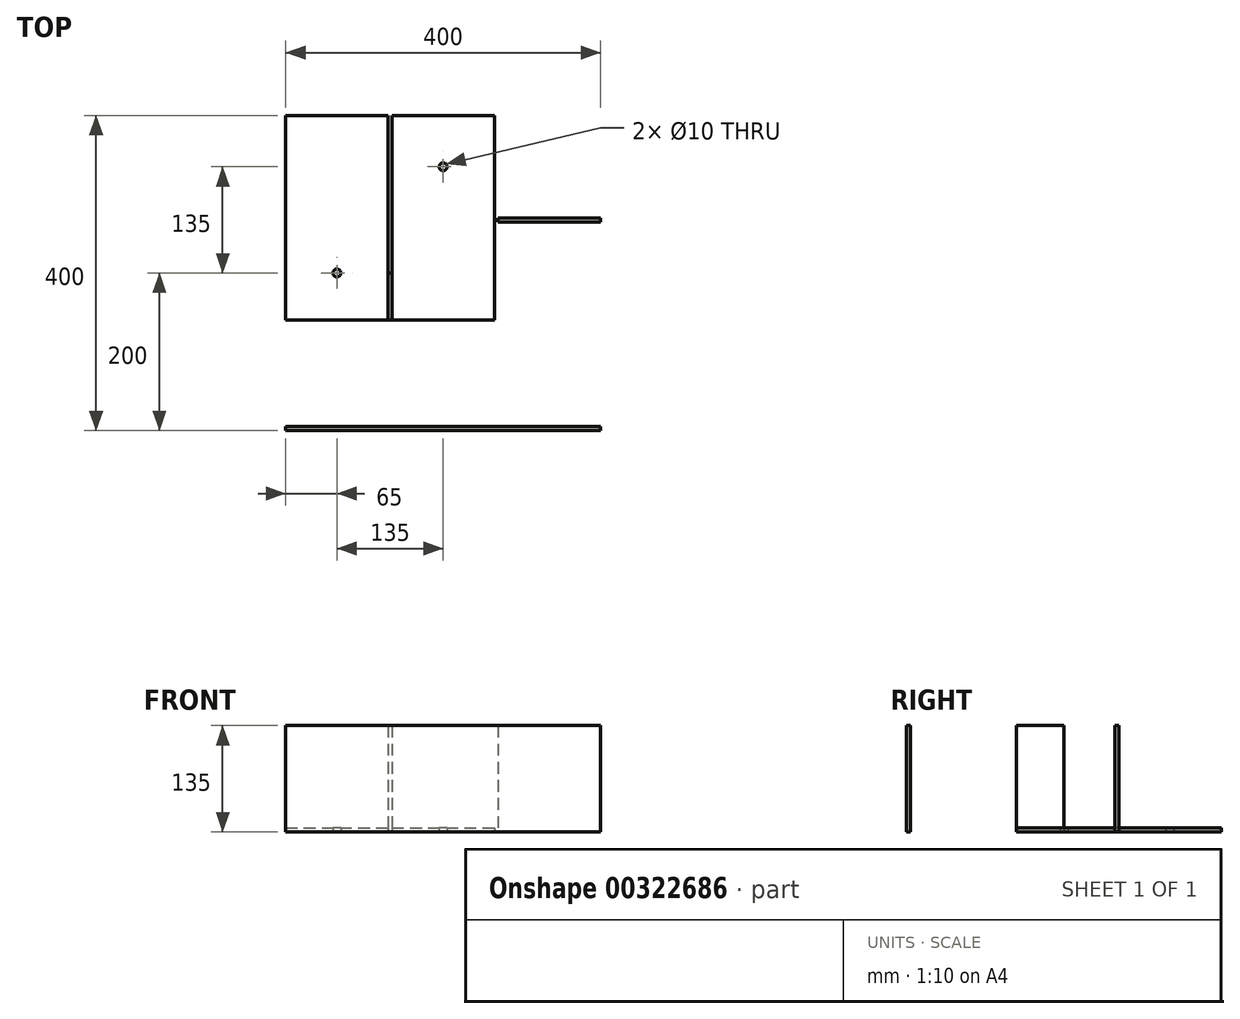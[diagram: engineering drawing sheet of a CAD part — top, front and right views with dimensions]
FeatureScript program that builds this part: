
annotation { "Feature Type Name" : "Feature", "Feature Type Description" : "" }
export const myFeature = defineFeature(function(context is Context, id is Id, definition is map)
    precondition{}
    {
        {
            var Q0;
            Q0=qCreatedBy(makeId("Top.planeOp"),FACE);
            var sketch = newSketch(context, id + "F0", { "sketchPlane" : qUnion([Q0])});
            skLineSegment(sketch, "E0", {"start": v(0, 0) * mm, "end": v(-200, 0) * mm});
            skLineSegment(sketch, "E1", {"start": v(-200, 0) * mm, "end": v(-200, 200) * mm});
            skLineSegment(sketch, "E2", {"start": v(-200, 0) * mm, "end": v(-200, -200) * mm});
            skLineSegment(sketch, "E3.bottom", {"start": v(-200, 200) * mm, "end": v(200, 200) * mm});
            skLineSegment(sketch, "E3.top", {"start": v(-200, -200) * mm, "end": v(200, -200) * mm});
            skLineSegment(sketch, "E3.left", {"start": v(-200, 200) * mm, "end": v(-200, -200) * mm});
            skLineSegment(sketch, "E3.right", {"start": v(200, 200) * mm, "end": v(200, -200) * mm});
            skLineSegment(sketch, "E4", {"start": v(-200, -200) * mm, "end": v(-200, -195) * mm});
            skLineSegment(sketch, "E5", {"start": v(-200, -195) * mm, "end": v(200, -195) * mm});
            skLineSegment(sketch, "E6", {"start": v(200, -195) * mm, "end": v(200, -200) * mm});
            skLineSegment(sketch, "E7", {"start": v(-200, -195) * mm, "end": v(-200, -65) * mm});
            skLineSegment(sketch, "E8", {"start": v(-200, -65) * mm, "end": v(-200, -60) * mm});
            skLineSegment(sketch, "E9", {"start": v(200, -65) * mm, "end": v(200, -60) * mm});
            skLineSegment(sketch, "E10", {"start": v(200, 200) * mm, "end": v(200, 70) * mm});
            skLineSegment(sketch, "E11", {"start": v(200, 70) * mm, "end": v(70, 70) * mm});
            skLineSegment(sketch, "E12", {"start": v(200, 70) * mm, "end": v(200, 65) * mm});
            skLineSegment(sketch, "E13", {"start": v(200, 65) * mm, "end": v(70, 65) * mm});
            skLineSegment(sketch, "E14", {"start": v(70, 70) * mm, "end": v(70, 65) * mm});
            skLineSegment(sketch, "E15", {"start": v(200, -195) * mm, "end": v(70, -195) * mm});
            skLineSegment(sketch, "E16", {"start": v(70, -195) * mm, "end": v(70, 200) * mm});
            skLineSegment(sketch, "E17", {"start": v(70, 200) * mm, "end": v(65, 200) * mm});
            skLineSegment(sketch, "E18", {"start": v(65, 200) * mm, "end": v(65, -195) * mm});
            skLineSegment(sketch, "E19", {"start": v(-200, -65) * mm, "end": v(65, -65) * mm});
            skLineSegment(sketch, "E20", {"start": v(-200, -60) * mm, "end": v(65, -60) * mm});
            skLineSegment(sketch, "E21", {"start": v(65, 200) * mm, "end": v(-65, 200) * mm});
            skLineSegment(sketch, "E22", {"start": v(-65, 200) * mm, "end": v(-65, -60) * mm});
            skLineSegment(sketch, "E23", {"start": v(-65, 200) * mm, "end": v(-70, 200) * mm});
            skLineSegment(sketch, "E24", {"start": v(-70, 200) * mm, "end": v(-70, -60) * mm});
            skLineSegment(sketch, "E25", {"start": v(70, -195) * mm, "end": v(65, -195) * mm});
            skLineSegment(sketch, "E26", {"start": v(0, 200) * mm, "end": v(0, 135) * mm});
            skPoint(sketch, "E26.endSnap0", {"position": v(200, 135) * mm});
            skLineSegment(sketch, "E27", {"start": v(-300.35, -32.4) * mm, "end": v(-291.76, -45.27) * mm});
            skLineSegment(sketch, "E28", {"start": v(-200, 0) * mm, "end": v(-135, 0) * mm});
            skLineSegment(sketch, "E29", {"start": v(0, -195) * mm, "end": v(0, -130) * mm});
            skLineSegment(sketch, "E30", {"start": v(200, 0) * mm, "end": v(135, 0) * mm});
            skPoint(sketch, "E30.endSnap0", {"position": v(200, 0) * mm});
            skCircle(sketch, "E31", {"center": v(135, 0) * mm, "radius": 5 * mm});
            skCircle(sketch, "E32", {"center": v(0, -130) * mm, "radius": 5 * mm});
            skCircle(sketch, "E33", {"center": v(-135, 0) * mm, "radius": 5 * mm});
            skCircle(sketch, "E34", {"center": v(0, 135) * mm, "radius": 5 * mm});
            skSolve(sketch);
        }
        {
            var Q0;
            {var subQ5=sQuery(id+"F0.wireOp",EDGE,"E23");Q0=makeQuery(id+"F0.imprint","IMPRINT",FACE,{"disambiguationData":[TD([[makeQuery(id+"F0.imprint","IMPRINT",EDGE,{"derivedFrom":subQ5}),1.0]])]});}
            var Q1;
            {var subQ0=sQuery(id+"F0.wireOp",EDGE,"E22");var subQ1=sQuery(id+"F0.wireOp",EDGE,"E0");var subQ2=makeQuery(id+"F0.imprint","INTERSECT",VERTEX,{"derivedFrom":[subQ1,subQ0]});Q1=makeQuery(id+"F0.imprint","IMPRINT",FACE,{"disambiguationData":[TD([[makeQuery(id+"F0.imprint","IMPRINT",EDGE,{"disambiguationData":[TD([[subQ2,-1.0]])],"derivedFrom":subQ1}),1.0]])]});}
            var Q2;
            {var subQ4=sQuery(id+"F0.wireOp",EDGE,"E8");Q2=makeQuery(id+"F0.imprint","IMPRINT",FACE,{"disambiguationData":[TD([[makeQuery(id+"F0.imprint","IMPRINT",EDGE,{"derivedFrom":subQ4}),-1.0]])]});}
            var Q3;
            Q3=makeQuery(id+"F0.imprint","IMPRINT",FACE,{"disambiguationData":[TD([[makeQuery(id+"F0.imprint","IMPRINT",EDGE,{"derivedFrom":sQuery(id+"F0.wireOp",EDGE,"E3.top")}),1.0]])]});
            var Q4;
            {var subQ0=sQuery(id+"F0.wireOp",EDGE,"E17");Q4=makeQuery(id+"F0.imprint","IMPRINT",FACE,{"disambiguationData":[TD([[makeQuery(id+"F0.imprint","IMPRINT",EDGE,{"derivedFrom":subQ0}),1.0]])]});}
            var Q5;
            {var subQ0=sQuery(id+"F0.wireOp",EDGE,"E11");Q5=makeQuery(id+"F0.imprint","IMPRINT",FACE,{"disambiguationData":[TD([[makeQuery(id+"F0.imprint","IMPRINT",EDGE,{"derivedFrom":subQ0}),1.0]])]});}
            extrude(context, id + "F1", {"entities" : qUnion([Q0, Q1, Q2, Q3, Q4, Q5]), "depth" : 135 * mm});
        }
        {
            var Q0;
            {var subQ0=sQuery(id+"F0.wireOp",EDGE,"E24");var subQ3=sQuery(id+"F0.wireOp",EDGE,"E0");var subQ4=makeQuery(id+"F0.imprint","INTERSECT",VERTEX,{"derivedFrom":[subQ3,subQ0]});Q0=makeQuery(id+"F0.imprint","IMPRINT",FACE,{"disambiguationData":[TD([[makeQuery(id+"F0.imprint","IMPRINT",EDGE,{"disambiguationData":[TD([[subQ4,-1.0]])],"derivedFrom":subQ3}),-1.0]])]});}
            var Q1;
            {var subQ0=sQuery(id+"F0.wireOp",EDGE,"E24");var subQ3=sQuery(id+"F0.wireOp",EDGE,"E0");var subQ4=makeQuery(id+"F0.imprint","INTERSECT",VERTEX,{"derivedFrom":[subQ3,subQ0]});Q1=makeQuery(id+"F0.imprint","IMPRINT",FACE,{"disambiguationData":[TD([[makeQuery(id+"F0.imprint","IMPRINT",EDGE,{"disambiguationData":[TD([[subQ4,-1.0]])],"derivedFrom":subQ3}),1.0]])]});}
            var Q2;
            {var subQ4=sQuery(id+"F0.wireOp",EDGE,"E7");Q2=makeQuery(id+"F0.imprint","IMPRINT",FACE,{"disambiguationData":[TD([[makeQuery(id+"F0.imprint","IMPRINT",EDGE,{"derivedFrom":subQ4}),-1.0]])]});}
            var Q3;
            Q3=makeQuery(id+"F0.imprint","IMPRINT",FACE,{"disambiguationData":[TD([[makeQuery(id+"F0.imprint","IMPRINT",EDGE,{"derivedFrom":sQuery(id+"F0.wireOp",EDGE,"E34")}),-1.0]])]});
            var Q4;
            {var subQ0=sQuery(id+"F0.wireOp",EDGE,"E9");Q4=makeQuery(id+"F0.imprint","IMPRINT",FACE,{"disambiguationData":[TD([[makeQuery(id+"F0.imprint","IMPRINT",EDGE,{"derivedFrom":subQ0}),1.0]])]});}
            var Q5;
            {var subQ0=sQuery(id+"F0.wireOp",EDGE,"E10");Q5=makeQuery(id+"F0.imprint","IMPRINT",FACE,{"disambiguationData":[TD([[makeQuery(id+"F0.imprint","IMPRINT",EDGE,{"derivedFrom":subQ0}),-1.0]])]});}
            extrude(context, id + "F2", {"entities" : qUnion([Q0, Q1, Q2, Q3, Q4, Q5]), "operationType" : NewBodyOperationType.ADD, "depth" : 5 * mm});
        }
    });
